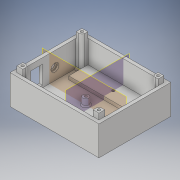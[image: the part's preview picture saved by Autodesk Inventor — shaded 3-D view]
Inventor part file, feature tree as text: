
AUTODESK INVENTOR PART (.ipt)
format: ipt  version: 2019 (Build 230136000, 136)  size: 304,128 bytes
history: native  units: in
note: dims shown in document units (in); Inventor stores cm internally (conversion verified against a paired STEP export)
features: thicken_offset x10, extrude x8, sketch x8, plane x3, chamfer x2, mirror x2, pattern_linear x1
ambient origin geometry x8: Origin, YZ Plane, XZ Plane, XY Plane, X Axis, Y Axis, Z Axis, Center Point
bodies: Solid1 (feature_tree)
feature tree (34):
  extrude  "Extrusion1"  Depth=2.8in
  extrude  "Extrusion2"  Depth=0.14in
  extrude  "Extrusion8"  Depth=0.14in
  pattern_linear  "Rectangular Pattern2"  Spacing1=0.599in  [1 undecoded]
  chamfer  "Chamfer2"  Distance=1.728in
  extrude  "Extrusion9"  Depth=3.01in
  plane  "Work Plane5"
  plane  "Work Plane6"
  extrude  "Extrusion12"  Depth=3.01in
  mirror  "Mirror9"
  mirror  "Mirror10"
  chamfer  "Chamfer3"  Distance=0.3in
  extrude  "Extrusion13"  Depth=3.01in
  thicken_offset  "Thicken1"
  thicken_offset  "Thicken2"
  thicken_offset  "Thicken3"
  thicken_offset  "Thicken4"
  thicken_offset  "Thicken5"
  thicken_offset  "Thicken6"
  thicken_offset  "Thicken7"
  thicken_offset  "Thicken8"
  thicken_offset  "Thicken9"
  thicken_offset  "Thicken10"
  extrude  "Extrusion15"  Depth=3.01in
  extrude  "Extrusion16"  Depth=3.01in TaperAngle=45.0deg
  sketch  "Sketch1"  dims[d0=3.527in d1=2.8in]
  sketch  "Sketch2"  dims[d2=0.14in d3=0.14in]
  sketch  "Sketch8"  dims[d4=0.14in d5=0.14in]
  sketch  "Sketch11"  dims[d6=1.119in d7=0.0in]
  sketch  "Sketch18"  dims[d8=0.14in]
  plane  "Work Plane7"
  sketch  "Sketch22"  dims[d9=0.0in]
  sketch  "Sketch24"  dims[d32=0.101in]
  sketch  "Sketch25"  dims[d33=0.2505in d34=0.599in d35=1.728in d36=0.819in d45=0.254in d46=0.3in d47=0.0in d48=0.7874in d50=1.728in d51=0.7874in d53=-0.819in d57=0.05in d58=0.125in d59=45.0deg d61=3.667in d63=0.247in d64=0.6295in d65=1.3in d66=0.494in d67=0.779in d68=0.75in d69=0.24in d71=1.259in d73=1.0in d74=0.0in d75=3.08in d98=-1.9035in d99=-1.54in d105=0.1185in d106=0.2585in d107=1.369in d108=0.0in d119=0.08in d120=0.125in d121=45.0deg d125=0.34in d126=0.07in d127=0.0in d131=0.008in d132=0.008in d133=0.008in d134=0.008in d135=0.008in d136=0.008in d137=0.008in d138=0.008in d139=0.008in d140=0.008in d141=0.008in d142=0.008in d143=0.008in d144=0.008in d145=0.008in d146=0.008in d147=0.008in d148=0.008in d149=0.008in d150=0.008in d151=2.996in d153=3.01in d155=0.14in d156=0.0in d157=0.112in d158=0.411in d159=1.503in d160=0.172in d161=0.0in d163=3.01in d164=0.828in]
note: 1 required parameter value undecoded (feature->parameter linkage not recoverable at this tier; creation-order binding heuristic only, values carry confidence <= 0.55)
